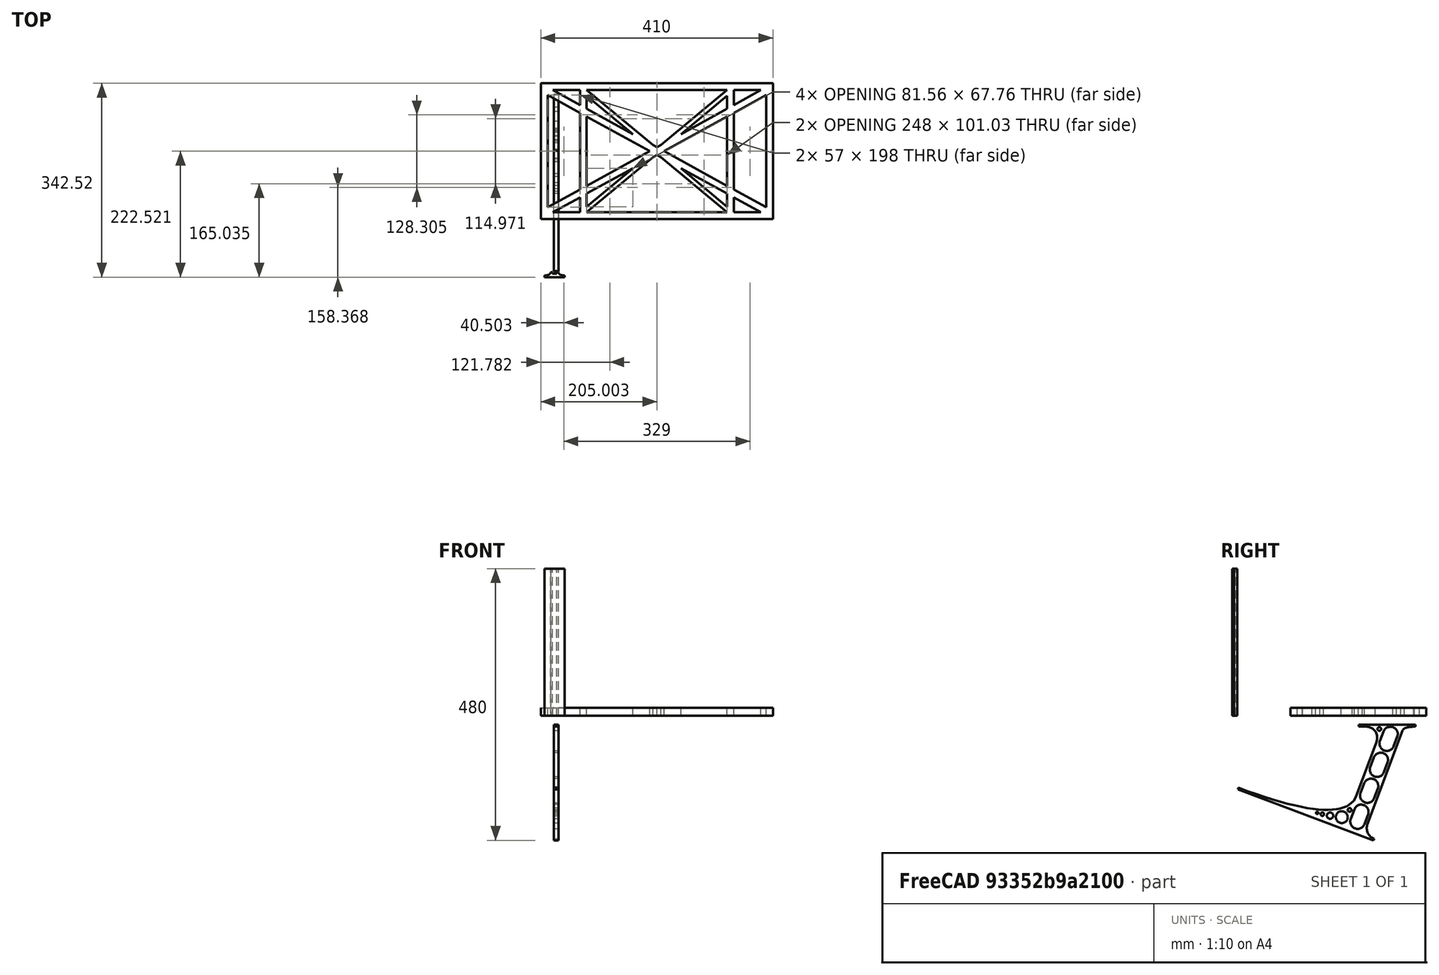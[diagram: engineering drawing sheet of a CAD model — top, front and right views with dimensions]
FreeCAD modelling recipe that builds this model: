
FCSTD DOCUMENT  (FreeCAD 0.19R0.19.2)
Label: laptopStand041
License: All rights reserved
LicenseURL: http://en.wikipedia.org/wiki/All_rights_reserved
objects: Sketcher::SketchObject×3, Part::Extrusion×3
note: 6 computed .brp shape members not serialized (recipe doc carries the construction recipe); baked Part::Feature solids carry a one-line shape summary decoded from their .brp

FEATURE [Sketcher::SketchObject] Sketch
  FullyConstrained = false
  sketch-geometry (55):
    g0: LineSegment StartX=-22.9272 StartY=136.221 StartZ=0 EndX=387.073 EndY=136.221 EndZ=0
    g1: LineSegment StartX=-22.9272 StartY=-103.779 StartZ=0 EndX=387.073 EndY=-103.779 EndZ=0
    g2: LineSegment StartX=387.073 StartY=136.221 StartZ=0 EndX=387.073 EndY=-103.779 EndZ=0
    g3: LineSegment StartX=375.073 StartY=115.221 StartZ=0 EndX=318.073 EndY=83.9235 EndZ=0
    g4: LineSegment StartX=-10.9272 StartY=-82.7794 StartZ=0 EndX=46.0728 EndY=-51.4823 EndZ=0
    g5: LineSegment StartX=-1.92719 StartY=124.221 StartZ=0 EndX=46.0728 EndY=97.8651 EndZ=0
    g6: LineSegment StartX=366.073 StartY=-91.7794 StartZ=0 EndX=318.073 EndY=-65.424 EndZ=0
    g7: LineSegment StartX=-10.9272 StartY=115.221 StartZ=0 EndX=-10.9272 EndY=-82.7794 EndZ=0
    g8: LineSegment StartX=375.073 StartY=-82.7794 StartZ=0 EndX=375.073 EndY=115.221 EndZ=0
    g9: LineSegment StartX=-1.92719 StartY=-91.7794 StartZ=0 EndX=46.0728 EndY=-91.7794 EndZ=0
    g10: LineSegment StartX=318.073 StartY=124.221 StartZ=0 EndX=366.073 EndY=124.221 EndZ=0
    g11: LineSegment StartX=306.073 StartY=-81.8102 StartZ=0 EndX=224.513 EndY=-14.0532 EndZ=0
    g12: LineSegment StartX=58.0728 StartY=114.251 StartZ=0 EndX=139.632 EndY=46.4944 EndZ=0
    g13: LineSegment StartX=306.073 StartY=124.221 StartZ=0 EndX=189.124 EndY=27.0628 EndZ=0
    g14: LineSegment StartX=58.0728 StartY=-91.7794 StartZ=0 EndX=175.022 EndY=5.37834 EndZ=0
    g15: LineSegment StartX=46.0728 StartY=124.221 StartZ=0 EndX=46.0728 EndY=97.8651 EndZ=0
    g16: LineSegment StartX=58.0728 StartY=-81.8102 StartZ=0 EndX=58.0728 EndY=-58.8351 EndZ=0
    g17: LineSegment StartX=318.073 StartY=124.221 StartZ=0 EndX=318.073 EndY=97.8651 EndZ=0
    g18: LineSegment StartX=306.073 StartY=114.251 StartZ=0 EndX=306.073 EndY=91.2763 EndZ=0
    g19: LineSegment StartX=182.073 StartY=23.1914 StartZ=0 EndX=189.124 EndY=27.0628 EndZ=0
    g20: LineSegment StartX=182.073 StartY=9.24976 StartZ=0 EndX=175.022 EndY=5.37834 EndZ=0
    g21: LineSegment StartX=224.513 StartY=46.4944 StartZ=0 EndX=306.073 EndY=114.251 EndZ=0
    g22: LineSegment StartX=175.022 StartY=27.0628 StartZ=0 EndX=58.0728 EndY=124.221 EndZ=0
    g23: LineSegment StartX=169.377 StartY=16.2206 StartZ=0 EndX=58.0728 EndY=77.3346 EndZ=0
    g24: LineSegment StartX=139.632 StartY=-14.0532 StartZ=0 EndX=58.0728 EndY=-81.8102 EndZ=0
    g25: LineSegment StartX=194.768 StartY=16.2206 StartZ=0 EndX=306.073 EndY=-44.8935 EndZ=0
    g26: LineSegment StartX=224.513 StartY=46.4944 StartZ=0 EndX=306.073 EndY=91.2763 EndZ=0
    g27: LineSegment StartX=175.022 StartY=27.0628 StartZ=0 EndX=182.073 EndY=23.1914 EndZ=0
    g28: LineSegment StartX=139.632 StartY=-14.0532 StartZ=0 EndX=58.0728 EndY=-58.8351 EndZ=0
    g29: LineSegment StartX=189.124 StartY=5.37834 StartZ=0 EndX=182.073 EndY=9.24976 EndZ=0
    g30: LineSegment StartX=189.124 StartY=5.37834 StartZ=0 EndX=306.073 EndY=-91.7794 EndZ=0
    g31: LineSegment StartX=306.073 StartY=77.3346 StartZ=0 EndX=306.073 EndY=-44.8935 EndZ=0
    g32: LineSegment StartX=318.073 StartY=83.9235 StartZ=0 EndX=318.073 EndY=-51.4823 EndZ=0
    g33: LineSegment StartX=318.073 StartY=97.8651 StartZ=0 EndX=366.073 EndY=124.221 EndZ=0
    g34: LineSegment StartX=306.073 StartY=77.3346 StartZ=0 EndX=194.768 EndY=16.2206 EndZ=0
    g35: LineSegment StartX=306.073 StartY=-58.8351 StartZ=0 EndX=224.513 EndY=-14.0532 EndZ=0
    g36: LineSegment StartX=306.073 StartY=-58.8351 StartZ=0 EndX=306.073 EndY=-81.8102 EndZ=0
    g37: LineSegment StartX=318.073 StartY=-51.4823 StartZ=0 EndX=375.073 EndY=-82.7794 EndZ=0
    g38: LineSegment StartX=318.073 StartY=-65.424 StartZ=0 EndX=318.073 EndY=-91.7794 EndZ=0
    g39: LineSegment StartX=306.073 StartY=124.221 StartZ=0 EndX=58.0728 EndY=124.221 EndZ=0
    g40: LineSegment StartX=318.073 StartY=-91.7794 StartZ=0 EndX=366.073 EndY=-91.7794 EndZ=0
    g41: LineSegment StartX=58.0728 StartY=-91.7794 StartZ=0 EndX=306.073 EndY=-91.7794 EndZ=0
    g42: LineSegment StartX=58.0728 StartY=-44.8935 StartZ=0 EndX=58.0728 EndY=77.3346 EndZ=0
    g43: LineSegment StartX=46.0728 StartY=-65.424 StartZ=0 EndX=-1.92719 EndY=-91.7794 EndZ=0
    g44: LineSegment StartX=46.0728 StartY=-65.424 StartZ=0 EndX=46.0728 EndY=-91.7794 EndZ=0
    g45: LineSegment StartX=58.0728 StartY=-44.8935 StartZ=0 EndX=169.377 EndY=16.2206 EndZ=0
    g46: LineSegment StartX=58.0728 StartY=91.2763 StartZ=0 EndX=58.0728 EndY=114.251 EndZ=0
    g47: LineSegment StartX=46.0728 StartY=83.9235 StartZ=0 EndX=46.0728 EndY=-51.4823 EndZ=0
    g48: LineSegment StartX=46.0728 StartY=124.221 StartZ=0 EndX=-1.92719 EndY=124.221 EndZ=0
    g49: LineSegment StartX=58.0728 StartY=91.2763 StartZ=0 EndX=139.632 EndY=46.4944 EndZ=0
    g50: LineSegment StartX=46.0728 StartY=83.9235 StartZ=0 EndX=-10.9272 EndY=115.221 EndZ=0
    g51: LineSegment StartX=-22.9272 StartY=136.221 StartZ=0 EndX=-42.9272 EndY=136.221 EndZ=0
    g52: LineSegment StartX=387.073 StartY=136.221 StartZ=0 EndX=407.073 EndY=136.221 EndZ=0
    g53: LineSegment StartX=-42.9272 StartY=136.221 StartZ=0 EndX=-42.9272 EndY=-103.779 EndZ=0
    g54: LineSegment StartX=-22.9272 StartY=-103.779 StartZ=0 EndX=-42.9272 EndY=-103.779 EndZ=0
  constraints (107):
    c: Horizontal(g0)
    c: Distance(g0) = 410
    c: Horizontal(g1)
    c: Coincident(g2,g0)
    c: Vertical(g2)
    c: Coincident(g1,g2)
    c: Block(g0)
    c: Horizontal(g9)
    c: Horizontal(g10)
    c: PointOnObject(g34,g5)
    c: Coincident(g27,g19)
    c: Coincident(g29,g20)
    c: Tangent(g6,g23)
    c: PointOnObject(g23,g4)
    c: PointOnObject(g25,g3)
    c: Coincident(g19,g13)
    c: Tangent(g19,g26)
    c: Coincident(g49,g12)
    c: Coincident(g27,g22)
    c: Coincident(g21,g26)
    c: Coincident(g20,g14)
    c: Coincident(g28,g24)
    c: Tangent(g20,g28)
    c: Coincident(g35,g11)
    c: Coincident(g30,g29)
    c: Coincident(g21,g18)
    c: Tangent(g18,g31)
    c: Tangent(g17,g32)
    c: Coincident(g26,g18)
    c: Tangent(g26,g33)
    c: Coincident(g3,g32)
    c: Coincident(g34,g31)
    c: Tangent(g3,g34)
    c: Coincident(g36,g11)
    c: Tangent(g6,g35)
    c: Tangent(g31,g36)
    c: Coincident(g25,g31)
    c: Tangent(g25,g37)
    c: Coincident(g32,g37)
    c: Coincident(g38,g6)
    c: Tangent(g32,g38)
    c: Coincident(g24,g16)
    c: Tangent(g16,g42)
    c: Coincident(g28,g16)
    c: Tangent(g28,g43)
    c: Coincident(g44,g43)
    c: Tangent(g15,g44)
    c: Coincident(g4,g47)
    c: Coincident(g45,g42)
    c: Tangent(g4,g45)
    c: Tangent(g42,g46)
    c: Tangent(g15,g47)
    c: Coincident(g12,g46)
    c: PointOnObject(g39,g22)
    c: Tangent(g39,g48)
    c: Coincident(g5,g15)
    c: Coincident(g49,g46)
    c: Tangent(g5,g49)
    c: Coincident(g23,g42)
    c: Coincident(g50,g47)
    c: Tangent(g23,g50)
    c: Block(g22)
    c: Block(g13)
    c: Block(g19)
    c: Block(g39)
    c: Block(g17)
    c: Block(g33)
    c: Block(g3)
    c: Block(g37)
    c: Block(g8)
    c: Block(g35)
    c: Block(g36)
    c: Block(g6)
    c: Block(g38)
    c: Block(g21)
    c: Block(g30)
    c: Block(g41)
    c: Block(g20)
    c: Block(g14)
    c: Block(g28)
    c: Block(g24)
    c: Block(g44)
    c: Block(g43)
    c: Block(g4)
    c: Block(g7)
    c: Block(g50)
    c: Block(g5)
    c: Block(g15)
    c: Block(g12)
    c: Block(g46)
    c: Block(g34)
    c: Block(g31)
    c: Block(g23)
    c: Block(g45)
    c: Block(g48)
    c: Block(g10)
    c: Block(g40)
    c: Block(g9)
    c: Horizontal(g51)
    c: Distance(g51) = 20
    c: Coincident(g52,g0)
    c: Horizontal(g52)
    c: Distance(g52) = 20
    c: Coincident(g53,g51)
    c: Vertical(g53)
    c: Horizontal(g54)
    c: Coincident(g54,g53)
FEATURE [Sketcher::SketchObject] Sketch001
  FullyConstrained = true
  MapMode = 4
  Placement = pos=(0,0,0) rot=(0.57735,0.57735,0.57735;2.0944rad)
  Support = -> [Sketch]
  sketch-geometry (46):
    g0: BSplineCurve PolesCount=3 KnotsCount=2 Degree=2 IsPeriodic=0
    g1: ArcOfCircle CenterX=73.122 CenterY=-32.2909 CenterZ=0 NormalX=0 NormalY=0 NormalZ=1 AngleXU=0 Radius=13 StartAngle=5.92268 EndAngle=9.06428
    g2: ArcOfCircle CenterX=66.7816 CenterY=-49.1439 CenterZ=0 NormalX=0 NormalY=0 NormalZ=1 AngleXU=0 Radius=13 StartAngle=2.78068 EndAngle=5.92131
    g3: ArcOfCircle CenterX=55.9263 CenterY=-78.1807 CenterZ=0 NormalX=0 NormalY=0 NormalZ=1 AngleXU=0 Radius=13 StartAngle=5.92268 EndAngle=9.06428
    g4: ArcOfCircle CenterX=49.5884 CenterY=-95.0342 CenterZ=0 NormalX=0 NormalY=0 NormalZ=1 AngleXU=0 Radius=13 StartAngle=2.78068 EndAngle=5.92131
    g5: ArcOfCircle CenterX=38.7206 CenterY=-124.067 CenterZ=0 NormalX=0 NormalY=0 NormalZ=1 AngleXU=0 Radius=13 StartAngle=5.92268 EndAngle=9.06428
    g6: ArcOfCircle CenterX=32.3875 CenterY=-140.92 CenterZ=0 NormalX=0 NormalY=0 NormalZ=1 AngleXU=0 Radius=13 StartAngle=2.78068 EndAngle=5.92131
    g7: ArcOfCircle CenterX=21.4715 CenterY=-169.934 CenterZ=0 NormalX=0 NormalY=0 NormalZ=1 AngleXU=0 Radius=13 StartAngle=5.92268 EndAngle=9.06428
    g8: ArcOfCircle CenterX=15.1336 CenterY=-186.787 CenterZ=0 NormalX=0 NormalY=0 NormalZ=1 AngleXU=0 Radius=13 StartAngle=2.78068 EndAngle=5.92131
    g9-g12: Circle x4 (B-spline internal-alignment scaffolding for g13; pole/knot coordinates omitted)
    g13: BSplineCurve PolesCount=4 KnotsCount=2 Degree=3 IsPeriodic=0
    g14: GeomPoint X=28.8094 Y=-19.0875 Z=0
    g15: GeomPoint X=47.0443 Y=-50.4712 Z=0
    g16: Circle CenterX=53.5586 CenterY=-23.2695 CenterZ=0 NormalX=0 NormalY=0 NormalZ=1 AngleXU=0 Radius=3.24518
    g17: Circle CenterX=-195.441 CenterY=-127.082 CenterZ=0 NormalX=0 NormalY=0 NormalZ=1 AngleXU=0 Radius=1
    g18: Circle CenterX=-8.24091 CenterY=-197.481 CenterZ=0 NormalX=0 NormalY=0 NormalZ=1 AngleXU=0 Radius=1
    g19: Circle CenterX=12.8789 CenterY=-141.321 CenterZ=0 NormalX=0 NormalY=0 NormalZ=1 AngleXU=0 Radius=1
    g20: BSplineCurve PolesCount=3 KnotsCount=2 Degree=2 IsPeriodic=0
    g21: GeomPoint X=-195.441 Y=-127.082 Z=0
    g22: GeomPoint X=12.8789 Y=-141.321 Z=0
    g23: Circle CenterX=-12.8016 CenterY=-179.036 CenterZ=0 NormalX=0 NormalY=0 NormalZ=1 AngleXU=0 Radius=10.5072
    g24: Circle CenterX=0.933922 CenterY=-166.43 CenterZ=0 NormalX=0 NormalY=0 NormalZ=1 AngleXU=0 Radius=3.26661
    g25: Circle CenterX=-33.5518 CenterY=-176.44 CenterZ=0 NormalX=0 NormalY=0 NormalZ=1 AngleXU=0 Radius=5.64388
    g26: Circle CenterX=-47.2366 CenterY=-173.859 CenterZ=0 NormalX=0 NormalY=0 NormalZ=1 AngleXU=0 Radius=3.01653
    g27: Circle CenterX=-56.2595 CenterY=-171.456 CenterZ=0 NormalX=0 NormalY=0 NormalZ=1 AngleXU=0 Radius=2.12826
    g28: ArcOfCircle CenterX=51.2151 CenterY=-198.473 CenterZ=0 NormalX=0 NormalY=0 NormalZ=1 AngleXU=0 Radius=20 StartAngle=2.78189 EndAngle=4.35269
    g29: LineSegment StartX=32.4951 StartY=-191.433 StartZ=0 EndX=94.6577 EndY=-26.1351 EndZ=0
    g30: LineSegment StartX=43.1192 StartY=-220.001 StartZ=0 EndX=-196.497 EndY=-129.89 EndZ=0
    g31: LineSegment StartX=43.1192 StartY=-220.001 StartZ=0 EndX=44.1752 EndY=-217.193 EndZ=0
    g32: LineSegment StartX=117.223 StartY=-19.0875 StartZ=0 EndX=117.223 EndY=-16.0875 EndZ=0
    g33: LineSegment StartX=117.223 StartY=-16.0875 StartZ=0 EndX=17.2232 EndY=-16.0875 EndZ=0
    g34: LineSegment StartX=17.2232 StartY=-16.0875 StartZ=0 EndX=17.2232 EndY=-19.0875 EndZ=0
    g35: LineSegment StartX=28.8094 StartY=-19.0875 StartZ=0 EndX=17.2232 EndY=-19.0875 EndZ=0
    g36: LineSegment StartX=47.0443 StartY=-50.4712 StartZ=0 EndX=12.8789 EndY=-141.321 EndZ=0
    g37: LineSegment StartX=-195.441 StartY=-127.082 StartZ=0 EndX=-196.497 EndY=-129.89 EndZ=0
    g38: LineSegment StartX=85.2864 StartY=-36.8765 StartZ=0 EndX=78.9396 EndY=-53.7463 EndZ=0
    g39: LineSegment StartX=60.9577 StartY=-27.7052 StartZ=0 EndX=54.6191 EndY=-44.5532 EndZ=0
    g40: LineSegment StartX=68.0907 StartY=-82.7664 StartZ=0 EndX=61.7465 EndY=-99.6365 EndZ=0
    g41: LineSegment StartX=43.7619 StartY=-73.595 StartZ=0 EndX=37.426 EndY=-90.4435 EndZ=0
    g42: LineSegment StartX=50.885 StartY=-128.652 StartZ=0 EndX=44.5456 EndY=-145.522 EndZ=0
    g43: LineSegment StartX=26.5562 StartY=-119.481 StartZ=0 EndX=20.2251 EndY=-136.329 EndZ=0
    g44: LineSegment StartX=9.3071 StartY=-165.349 StartZ=0 EndX=2.97115 EndY=-182.197 EndZ=0
    g45: LineSegment StartX=33.6358 StartY=-174.52 StartZ=0 EndX=27.2917 EndY=-191.39 EndZ=0
  constraints (70):
    c: Block(g0)
    c: Block(g1)
    c: Block(g2)
    c: Block(g4)
    c: Block(g3)
    c: Block(g6)
    c: Block(g5)
    c: Block(g8)
    c: Block(g7)
    c: Weight(g9) = 1
    c: Equal(g9,g10)
    c: Equal(g9,g11)
    c: Equal(g9,g12)
    c: InternalAlignment(g9-g12 -> g13) x4
    c: InternalAlignment(g14,g13)
    c: InternalAlignment(g15,g13)
    c: Block(g16)
    c: Weight(g17) = 1
    c: Equal(g17,g18)
    c: Equal(g17,g19)
    c: InternalAlignment(g17,g20)
    c: InternalAlignment(g18,g20)
    c: InternalAlignment(g19,g20)
    c: InternalAlignment(g21,g20)
    c: InternalAlignment(g22,g20)
    c: Block(g20)
    c: Block(g23)
    c: Block(g24)
    c: Block(g25)
    c: Block(g26)
    c: Block(g27)
    c: Block(g28)
    c: Coincident(g29,g28)
    c: Coincident(g29,g0)
    c: Block(g13)
    c: Coincident(g31,g30)
    c: Coincident(g31,g28)
    c: Block(g31)
    c: Coincident(g32,g0)
    c: Vertical(g32)
    c: Coincident(g33,g32)
    c: Horizontal(g33)
    c: Coincident(g34,g33)
    c: Vertical(g34)
    c: Block(g33)
    c: Coincident(g35,g13)
    c: Coincident(g35,g34)
    c: Horizontal(g35)
    c: Coincident(g36,g13)
    c: Coincident(g36,g20)
    c: Coincident(g37,g20)
    c: Coincident(g37,g30)
    c: Block(g30)
    c: Coincident(g38,g1)
    c: Coincident(g38,g2)
    c: Coincident(g39,g1)
    c: Coincident(g39,g2)
    c: Coincident(g40,g3)
    c: Coincident(g40,g4)
    c: Coincident(g41,g3)
    c: Coincident(g41,g4)
    c: Coincident(g42,g5)
    c: Coincident(g42,g6)
    c: Coincident(g43,g5)
    c: Coincident(g43,g6)
    c: Coincident(g44,g7)
    c: Coincident(g44,g8)
    c: Coincident(g45,g7)
    c: Coincident(g45,g8)
    c: Distance(g30) = 256
FEATURE [Part::Extrusion] Extrude002
  Base = -> Sketch001
  Dir = (1,0,0)
  DirMode = 2
  FaceMakerClass = Part::FaceMakerBullseye
  LengthFwd = 8
  LengthRev = 0
  Solid = true
  Symmetric = false
FEATURE [Sketcher::SketchObject] Sketch002
  FullyConstrained = true
  sketch-geometry (20):
    g0: LineSegment StartX=-2.77179 StartY=-200.304 StartZ=0 EndX=5.22821 EndY=-200.304 EndZ=0
    g1: LineSegment StartX=5.22821 StartY=-200.304 StartZ=0 EndX=5.22821 EndY=-197.304 EndZ=0
    g2: LineSegment StartX=-2.77179 StartY=-200.304 StartZ=0 EndX=-2.77179 EndY=-197.304 EndZ=0
    g3: LineSegment StartX=5.22821 StartY=-197.304 StartZ=0 EndX=8.22821 EndY=-197.304 EndZ=0
    g4: LineSegment StartX=-2.77179 StartY=-197.304 StartZ=0 EndX=-5.77179 EndY=-197.304 EndZ=0
    g5: LineSegment StartX=19.2282 StartY=-203.304 StartZ=0 EndX=19.2282 EndY=-206.304 EndZ=0
    g6: LineSegment StartX=-16.7718 StartY=-203.304 StartZ=0 EndX=-16.7718 EndY=-206.304 EndZ=0
    g7: LineSegment StartX=-16.7718 StartY=-206.304 StartZ=0 EndX=19.2282 EndY=-206.304 EndZ=0
    g8: Circle CenterX=-16.7718 CenterY=-203.304 CenterZ=0 NormalX=0 NormalY=0 NormalZ=1 AngleXU=0 Radius=1
    g9: Circle CenterX=-5.77179 CenterY=-203.304 CenterZ=0 NormalX=0 NormalY=0 NormalZ=1 AngleXU=0 Radius=1
    g10: Circle CenterX=-5.77179 CenterY=-197.304 CenterZ=0 NormalX=0 NormalY=0 NormalZ=1 AngleXU=0 Radius=1
    g11: BSplineCurve PolesCount=3 KnotsCount=2 Degree=2 IsPeriodic=0
    g12: GeomPoint X=-16.7718 Y=-203.304 Z=0
    g13: GeomPoint X=-5.77179 Y=-197.304 Z=0
    g14: Circle CenterX=19.2282 CenterY=-203.304 CenterZ=0 NormalX=0 NormalY=0 NormalZ=1 AngleXU=0 Radius=1
    g15: Circle CenterX=8.22821 CenterY=-203.304 CenterZ=0 NormalX=0 NormalY=0 NormalZ=1 AngleXU=0 Radius=1
    g16: Circle CenterX=8.22821 CenterY=-197.304 CenterZ=0 NormalX=0 NormalY=0 NormalZ=1 AngleXU=0 Radius=1
    g17: BSplineCurve PolesCount=3 KnotsCount=2 Degree=2 IsPeriodic=0
    g18: GeomPoint X=19.2282 Y=-203.304 Z=0
    g19: GeomPoint X=8.22821 Y=-197.304 Z=0
  constraints (41):
    c: Horizontal(g0)
    c: Distance(g0) = 8
    c: Coincident(g1,g0)
    c: Vertical(g1)
    c: Distance(g1) = 3
    c: Coincident(g2,g0)
    c: Vertical(g2)
    c: Distance(g2) = 3
    c: Coincident(g3,g1)
    c: Horizontal(g3)
    c: Distance(g3) = 3
    c: Coincident(g4,g2)
    c: Horizontal(g4)
    c: Distance(g4) = 3
    c: Vertical(g5)
    c: Vertical(g6)
    c: Coincident(g7,g6)
    c: Coincident(g7,g5)
    c: Weight(g8) = 1
    c: Equal(g8,g9)
    c: Equal(g8,g10)
    c: Coincident(g11,g4)
    c: InternalAlignment(g8,g11)
    c: InternalAlignment(g9,g11)
    c: InternalAlignment(g10,g11)
    c: InternalAlignment(g12,g11)
    c: InternalAlignment(g13,g11)
    c: Coincident(g17,g5)
    c: Weight(g14) = 1
    c: Equal(g14,g15)
    c: Equal(g14,g16)
    c: Coincident(g17,g3)
    c: InternalAlignment(g14,g17)
    c: InternalAlignment(g15,g17)
    c: InternalAlignment(g16,g17)
    c: InternalAlignment(g18,g17)
    c: InternalAlignment(g19,g17)
    c: Block(g7)
    c: Block(g17)
    c: Block(g11)
    c: Block(g6)
FEATURE [Part::Extrusion] Extrude003
  Base = -> Sketch002
  Dir = (0,0,1)
  DirMode = 2
  FaceMakerClass = Part::FaceMakerBullseye
  LengthFwd = 260
  LengthRev = 0
  Solid = true
  Symmetric = false
FEATURE [Part::Extrusion] Extrude
  Base = -> Sketch
  Dir = (0,0,1)
  DirMode = 2
  FaceMakerClass = Part::FaceMakerBullseye
  LengthFwd = 14
  LengthRev = 0
  Solid = true
  Symmetric = false
